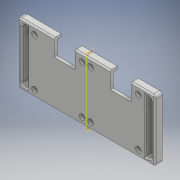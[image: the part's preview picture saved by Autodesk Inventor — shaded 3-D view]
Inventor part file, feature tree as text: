
AUTODESK INVENTOR PART (.ipt)
format: ipt  version: 2017 (Build 210142000, 142)  size: 273,408 bytes
history: native  units: mm
features: extrude x5, sketch x5, fillet x3, mirror x2, chamfer x2, projected_geometry x2, pattern_linear x1, hole x1
ambient origin geometry x8: Origin, YZ Plane, XZ Plane, XY Plane, X Axis, Y Axis, Z Axis, Center Point
bodies: Solid1 (feature_tree)
feature tree (21):
  extrude  "Extrusion1"  Depth=98.0mm
  extrude  "Extrusion2"  Depth=40.0mm
  extrude  "Extrusion3"  TaperAngle=0.0deg  [1 undecoded]
  extrude  "Extrusion5"  Depth=6.0mm
  extrude  "Extrusion6"  Depth=6.0mm
  pattern_linear  "Rectangular Pattern1"  Spacing1=6.0mm  [1 undecoded]
  mirror  "Mirror2"
  chamfer  "Chamfer3"  Distance=6.0mm
  fillet  "Fillet4"  Radius=6.0mm
  fillet  "Fillet5"  Radius=6.0mm
  fillet  "Fillet6"  Radius=2.0mm
  chamfer  "Chamfer4"  Distance=38.0mm
  hole  "Hole1"  [1 undecoded]
  mirror  "Mirror3"
  sketch  "Sketch1"  dims[d0=44.0mm d1=98.0mm]
  sketch  "Sketch2"  dims[d2=5.0mm d3=0.0mm d4=40.0mm]
  sketch  "Sketch3"  dims[d5=40.0mm d6=0.0mm]
  projected_geometry  "Projected Loop1"
  sketch  "Sketch5"  dims[d7=3.0mm d8=0.0mm d9=6.0mm]
  projected_geometry  "Projected Loop3"
  sketch  "Sketch8"  dims[d10=6.0mm d11=6.0mm d12=6.0mm d13=6.0mm d14=6.0mm d15=6.0mm d16=2.0mm d17=0.0mm d25=38.0mm d26=2.0mm d27=4.0mm d28=2.0mm d29=0.0mm d38=10.0mm d39=15.0mm d40=8.0mm d41=10.0mm d42=0.0mm d43=20.0mm d45=40.0mm d46=1.0mm d47=2.0mm d48=45.0deg d49=2.0mm d50=2.0mm d51=2.0mm d52=1.0mm d53=2.0mm d54=45.0deg d59=34.0mm d60=34.0mm d61=20.0mm d62=2.0mm d63=6.0mm d64=4.0mm d65=2.0mm d66=90.0deg d67=10.0mm d68=20.594885mm d69=6.0mm d70=10.0mm]
note: 3 required parameter values undecoded (feature->parameter linkage not recoverable at this tier; creation-order binding heuristic only, values carry confidence <= 0.55)
